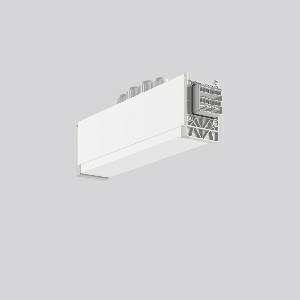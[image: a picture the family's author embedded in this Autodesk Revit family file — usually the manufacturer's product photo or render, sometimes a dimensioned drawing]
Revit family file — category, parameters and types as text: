
# Revit family: linedo_mitteleinspeisung_7pol_982698_012_3_7933
name_source: partatom
category: Lighting Fixtures
units: mm (PartAtom-declared; Revit-internal decimal feet)

## family parameters
Cut with Voids When Loaded = No
Host = Face
Light Source = No
Part Type = Normal
Room Calculation Point = No
Round Connector Dimension = Use Diameter
Shared = No

## types (1)
- LINEDO_Mitteleinspeisung_7pol
    Apparent Load = 0 VA
    Default Elevation = 1800 mm
    Description = Series: LINEDO
Middle power feed, 7-pole, connection socket / plug. Housing: extruded aluminium profile, powder-coated. Cover made of plastic, surface like housing. LINEDO plug system, plastic, light grey. 4 cable glands (2 x M20 and 2 x M25). Cable glands on top. Easy connection for rigid or flexible wires. Especially for use with continuous line modules with high opal diffuser.
Colour: white
Length: 330 mm
Width: 58 mm
Height: 91 mm
Weight: 801 g
    Height = 91 mm
    Lamp = 0 x
    Length = 330 mm
    Luminous efficacy = 0 lm/W
    Manufacturer = RZB
    ModVariant = No
    Model = 982698.012.3
    Mounting Place = Ceiling
    Mounting Type = Surface mounted
    Number of Poles = 1
    OnlyDefault = Yes
    Power Factor = 1
    Product Name = LINEDO_Mitteleinspeisung_7pol
    Product group = Continuous line luminaire system Linedo IP 54
    ProductGroupID = 314
    Protection Class = Protection class I
    Protection Degree = Degree of protection
    RLX_Detail_Level = 1
    RLX_Emergency_Light_Flux = 0 lm
    RLX_Emergency_Type = 0
    RLX_Emergency_Type_DB = No
    RlxData = <blob elided: 21965 chars, md5=cd20ce53>
    Standby Power = 0 W
    System Light Flux = 0 lm
    System Power = 0 W
    Type Comments = Product without accessories
    Type Image = 982698.012.jpg
    URL = http://relux.com
    VarID = ---
    Voltage = 0 V
    Weight = 0.00 kg
    Width = 58 mm

## geometry (parser evidence)
native form markers: Blend x4, Sweep x13
no freeform markers — native parametric forms only
